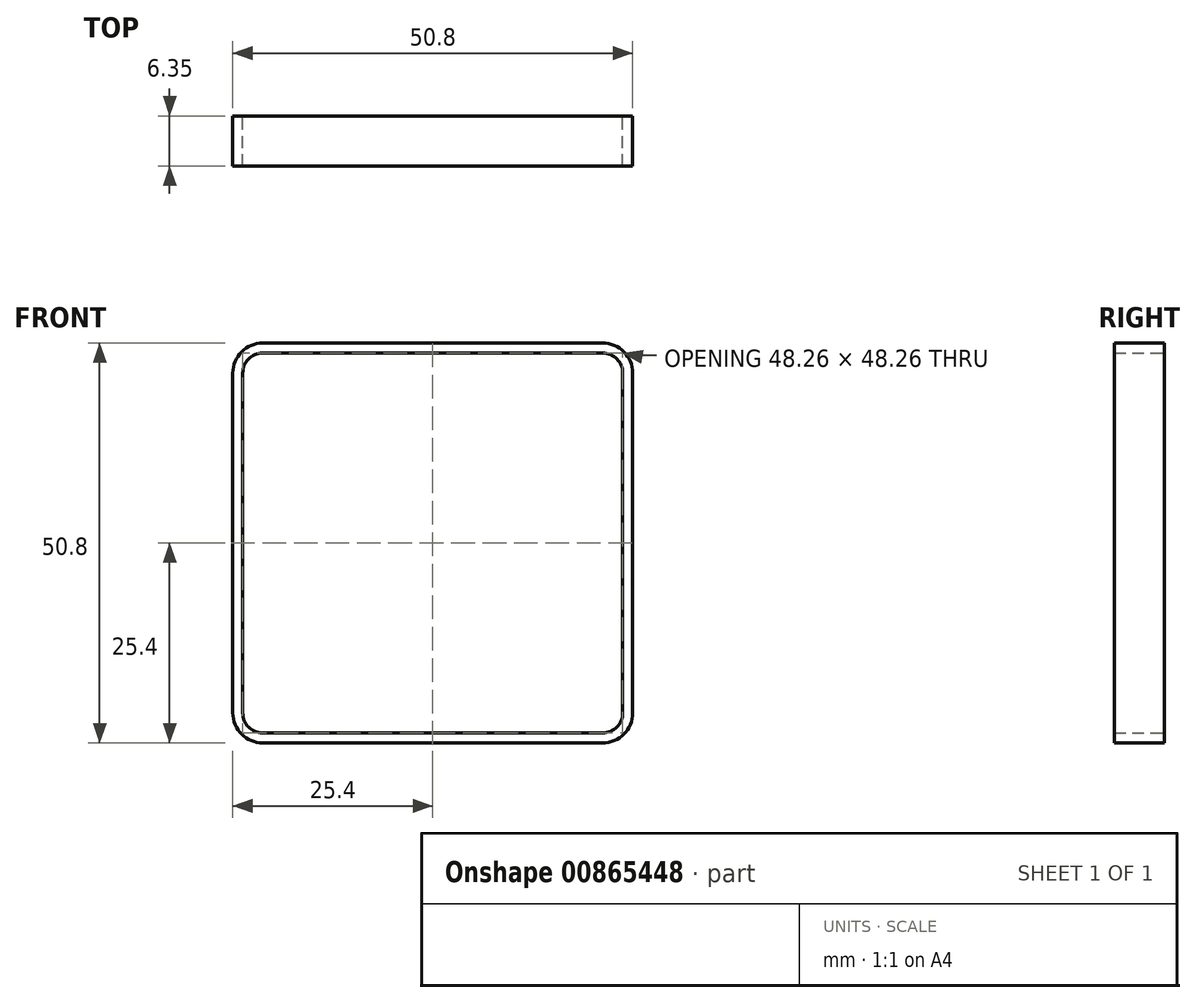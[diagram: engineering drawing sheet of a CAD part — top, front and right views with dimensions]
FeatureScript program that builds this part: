
annotation { "Feature Type Name" : "Feature", "Feature Type Description" : "" }
export const myFeature = defineFeature(function(context is Context, id is Id, definition is map)
    precondition{}
    {
        {
            var Q0;
            Q0=qCreatedBy(makeId("Front.planeOp"),FACE);
            var sketch = newSketch(context, id + "F0", { "sketchPlane" : qUnion([Q0])});
            skLineSegment(sketch, "E0", {"start": v(3.81, 0) * mm, "end": v(47, 0) * mm});
            skLineSegment(sketch, "E1", {"start": v(50.8, 3.81) * mm, "end": v(50.8, 46.99) * mm});
            skLineSegment(sketch, "E2", {"start": v(47, 50.8) * mm, "end": v(3.81, 50.8) * mm});
            skLineSegment(sketch, "E3", {"start": v(0, 46.99) * mm, "end": v(0, 3.81) * mm});
            skPoint(sketch, "E4.visualSharp", {"position": v(0, 50.8) * mm});
            skArc(sketch, "E4.filletArc", {"start": v(3.81, 50.8) * mm, "mid": v(1.12, 49.68) * mm, "end": v(0, 46.99) * mm});
            skPoint(sketch, "E5.visualSharp", {"position": v(50.8, 50.8) * mm});
            skArc(sketch, "E5.filletArc", {"start": v(50.8, 46.99) * mm, "mid": v(49.68, 49.68) * mm, "end": v(47, 50.8) * mm});
            skPoint(sketch, "E6.visualSharp", {"position": v(0, 0) * mm});
            skArc(sketch, "E6.filletArc", {"start": v(0, 3.81) * mm, "mid": v(1.12, 1.12) * mm, "end": v(3.81, 0) * mm});
            skPoint(sketch, "E7.visualSharp", {"position": v(50.8, 0) * mm});
            skArc(sketch, "E7.filletArc", {"start": v(47, 0) * mm, "mid": v(49.68, 1.12) * mm, "end": v(50.8, 3.81) * mm});
            skSolve(sketch);
        }
        {
            var Q0;
            Q0=makeQuery(id+"F0.imprint","IMPRINT",FACE,{"disambiguationData":[TD([[makeQuery(id+"F0.imprint","IMPRINT",EDGE,{"derivedFrom":sQuery(id+"F0.wireOp",EDGE,"E0")}),1.0]])]});
            extrude(context, id + "F1", {"entities" : qUnion([Q0]), "depth" : 6.35 * mm, "offsetDistance" : 25.4 * mm});
        }
        {
            var Q0;
            Q0=makeQuery(id+"F1.opExtrude","CAP_FACE",FACE,{"disambiguationData":[OSD([sQuery(id+"F0.wireOp",EDGE,"E0"),sQuery(id+"F0.wireOp",EDGE,"E1"),sQuery(id+"F0.wireOp",EDGE,"E2"),sQuery(id+"F0.wireOp",EDGE,"E3"),sQuery(id+"F0.wireOp",EDGE,"E4.filletArc"),sQuery(id+"F0.wireOp",EDGE,"E5.filletArc"),sQuery(id+"F0.wireOp",EDGE,"E6.filletArc"),sQuery(id+"F0.wireOp",EDGE,"E7.filletArc")])],"isStart":false});
            var Q1;
            Q1=makeQuery(id+"F1.opExtrude","CAP_FACE",FACE,{"disambiguationData":[OSD([sQuery(id+"F0.wireOp",EDGE,"E0"),sQuery(id+"F0.wireOp",EDGE,"E1"),sQuery(id+"F0.wireOp",EDGE,"E2"),sQuery(id+"F0.wireOp",EDGE,"E3"),sQuery(id+"F0.wireOp",EDGE,"E4.filletArc"),sQuery(id+"F0.wireOp",EDGE,"E5.filletArc"),sQuery(id+"F0.wireOp",EDGE,"E6.filletArc"),sQuery(id+"F0.wireOp",EDGE,"E7.filletArc")])],"isStart":true});
            shell(context, id + "F2", {"entities" : qUnion([Q0, Q1]), "thickness" : 1.27 * mm});
        }
    });
